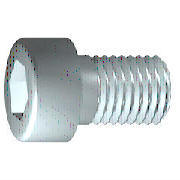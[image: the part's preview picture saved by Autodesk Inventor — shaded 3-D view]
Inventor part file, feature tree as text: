
AUTODESK INVENTOR PART (.ipt)
format: ipt  version: 2017 (Build 210142000, 142)  size: 186,880 bytes
history: native  units: mm (DEFAULTED — no unit token found)
features: sketch x2, extrude x1, plane x1, fillet x1
ambient origin geometry x7: Origin, YZ Plane, XY Plane, X Axis, Y Axis, Z Axis, Center Point
bodies: Solid1 (feature_tree), Body (feature_tree)
feature tree (5):
  extrude  "Slot"  Depth=3.0mm
  plane  "Work Plane1"
  fillet  "Fillet2"  Radius=3.0mm
  sketch  "Sketch1"  dims[d1=14.693275mm d2=0.306825mm d3=3.0mm]
  sketch  "Sketch2"  dims[d4=1.5mm d5=60.0deg d6=3.0mm d7=3.0mm d8=2.886751mm d9=5.5mm d10=90.0deg d11=10.0mm d12=0.0mm d13=14.693275mm d14=0.0mm d15=0.306725mm d16=0.306725mm d17=0.3mm d19=0.0mm d26=16.0mm d27=45.0deg d28=0.0mm d29=0.0mm d30=0.1mm]
